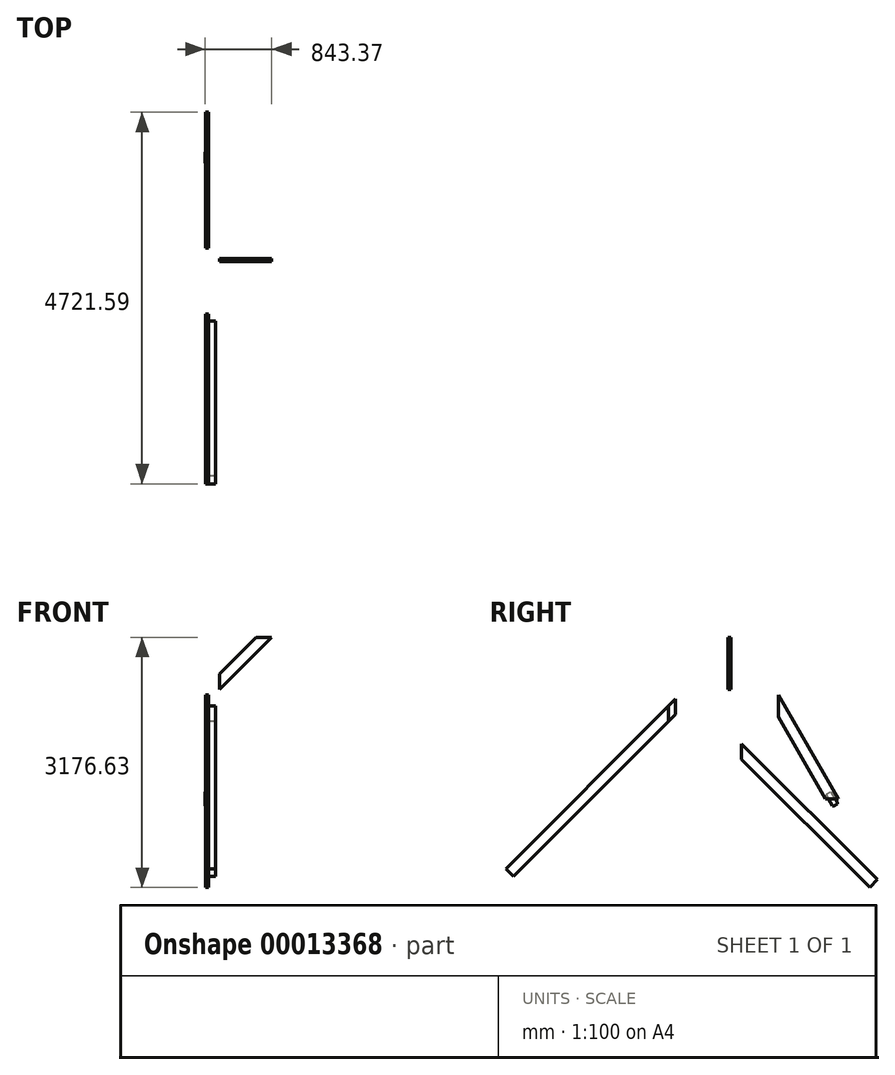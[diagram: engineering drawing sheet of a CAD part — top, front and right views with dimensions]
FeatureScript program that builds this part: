
annotation { "Feature Type Name" : "Feature", "Feature Type Description" : "" }
export const myFeature = defineFeature(function(context is Context, id is Id, definition is map)
    precondition{}
    {
        {
            var Q0;
            Q0=qCreatedBy(makeId("Front.planeOp"),FACE);
            var sketch = newSketch(context, id + "F0", { "sketchPlane" : qUnion([Q0])});
            skLineSegment(sketch, "E0", {"start": v(181.36, 197.57) * mm, "end": v(644.2, 660.4) * mm});
            skLineSegment(sketch, "E1", {"start": v(644.2, 660.4) * mm, "end": v(841.76, 660.4) * mm});
            skLineSegment(sketch, "E2", {"start": v(841.76, 660.4) * mm, "end": v(181.36, 0) * mm});
            skLineSegment(sketch, "E3", {"start": v(181.36, 0) * mm, "end": v(181.36, 197.57) * mm});
            skLineSegment(sketch, "E4", {"start": v(181.36, 0) * mm, "end": v(935.54, 0) * mm, "construction": true});
            skSolve(sketch);
        }
        {
            var Q0;
            Q0=makeQuery(id+"F0.imprint","IMPRINT",FACE,{"disambiguationData":[TD([[makeQuery(id+"F0.imprint","IMPRINT",EDGE,{"derivedFrom":sQuery(id+"F0.wireOp",EDGE,"E0")}),-1.0]])]});
            extrude(context, id + "F1", {"entities" : qUnion([Q0]), "depth" : 38.1 * mm});
        }
        {
            var Q0;
            Q0=qCreatedBy(makeId("Right.planeOp"),FACE);
            var sketch = newSketch(context, id + "F2", { "sketchPlane" : qUnion([Q0])});
            skLineSegment(sketch, "E5", {"start": v(-705.66, -124.36) * mm, "end": v(-705.66, -321.92) * mm});
            skLineSegment(sketch, "E6", {"start": v(-705.66, -321.92) * mm, "end": v(-2762.14, -2378.4) * mm});
            skLineSegment(sketch, "E7", {"start": v(-2762.14, -2378.4) * mm, "end": v(-2860.92, -2279.62) * mm});
            skLineSegment(sketch, "E8", {"start": v(-2860.92, -2279.62) * mm, "end": v(-705.66, -124.36) * mm});
            skSolve(sketch);
        }
        {
            var Q0;
            Q0=qSketchRegion(id+"F2",true);
            extrude(context, id + "F3", {"entities" : qUnion([Q0]), "depth" : 38.1 * mm});
        }
        {
            var Q0;
            Q0=qCreatedBy(makeId("Right.planeOp"),FACE);
            var sketch = newSketch(context, id + "F4", { "sketchPlane" : qUnion([Q0])});
            skLineSegment(sketch, "E9", {"start": v(136.46, -693.23) * mm, "end": v(136.46, -890.8) * mm});
            skLineSegment(sketch, "E10", {"start": v(136.46, -890.8) * mm, "end": v(1761.89, -2516.23) * mm});
            skLineSegment(sketch, "E11", {"start": v(1761.89, -2516.23) * mm, "end": v(1860.67, -2417.44) * mm});
            skLineSegment(sketch, "E12", {"start": v(1860.67, -2417.44) * mm, "end": v(136.46, -693.23) * mm});
            skSolve(sketch);
        }
        {
            var Q0;
            Q0=qSketchRegion(id+"F4",true);
            extrude(context, id + "F5", {"entities" : qUnion([Q0]), "depth" : 38.1 * mm});
        }
        {
            var Q0;
            Q0=qCreatedBy(makeId("Right.planeOp"),FACE);
            var sketch = newSketch(context, id + "F6", { "sketchPlane" : qUnion([Q0])});
            skLineSegment(sketch, "E13", {"start": v(601.15, -72.16) * mm, "end": v(601.15, -351.56) * mm});
            skLineSegment(sketch, "E14", {"start": v(601.15, -351.56) * mm, "end": v(1201.84, -1391.98) * mm});
            skLineSegment(sketch, "E15", {"start": v(1201.84, -1391.98) * mm, "end": v(1363.15, -1391.98) * mm});
            skLineSegment(sketch, "E16", {"start": v(1363.15, -1391.98) * mm, "end": v(601.15, -72.16) * mm});
            skSolve(sketch);
        }
        {
            var Q0;
            Q0=qSketchRegion(id+"F6",true);
            extrude(context, id + "F7", {"entities" : qUnion([Q0]), "depth" : 38.1 * mm});
        }
        {
            var Q0;
            Q0=makeQuery(id+"F7.opExtrude","CAP_FACE",FACE,{"disambiguationData":[OSD([sQuery(id+"F6.wireOp",EDGE,"E13"),sQuery(id+"F6.wireOp",EDGE,"E14"),sQuery(id+"F6.wireOp",EDGE,"E15"),sQuery(id+"F6.wireOp",EDGE,"E16")])],"isStart":true});
            var sketch = newSketch(context, id + "F8", { "sketchPlane" : qUnion([Q0])});
            skLineSegment(sketch, "E17", {"start": v(-1206.16, -1335.97) * mm, "end": v(-1295.06, -1489.95) * mm});
            skLineSegment(sketch, "E18", {"start": v(-1361.05, -1451.85) * mm, "end": v(-1295.06, -1489.95) * mm});
            skLineSegment(sketch, "E19", {"start": v(-1361.05, -1451.85) * mm, "end": v(-1272.15, -1297.87) * mm});
            skLineSegment(sketch, "E20", {"start": v(-1206.16, -1335.97) * mm, "end": v(-1272.15, -1297.87) * mm});
            skLineSegment(sketch, "E21", {"start": v(-1299.65, -1282) * mm, "end": v(-1178.66, -1351.85) * mm, "construction": true});
            skPoint(sketch, "E22", {"position": v(-1239.16, -1316.92) * mm});
            skSolve(sketch);
        }
        {
            var Q0;
            Q0=qSketchRegion(id+"F8",true);
            extrude(context, id + "F9", {"entities" : qUnion([Q0]), "depth" : 1.61 * mm});
        }
        {
            var Q0;
            Q0=makeQuery(id+"F9.opExtrude","SWEPT_EDGE",EDGE,{"disambiguationData":[OSD([sQuery(id+"F8.wireOp",EDGE,"E19"),sQuery(id+"F8.wireOp",EDGE,"E20")])]});
            var Q1;
            Q1=makeQuery(id+"F9.opExtrude","SWEPT_EDGE",EDGE,{"disambiguationData":[OSD([sQuery(id+"F8.wireOp",EDGE,"E17"),sQuery(id+"F8.wireOp",EDGE,"E20")])]});
            var Q2;
            Q2=makeQuery(id+"F9.opExtrude","SWEPT_EDGE",EDGE,{"disambiguationData":[OSD([sQuery(id+"F8.wireOp",EDGE,"E17"),sQuery(id+"F8.wireOp",EDGE,"E18")])]});
            var Q3;
            Q3=makeQuery(id+"F9.opExtrude","SWEPT_EDGE",EDGE,{"disambiguationData":[OSD([sQuery(id+"F8.wireOp",EDGE,"E18"),sQuery(id+"F8.wireOp",EDGE,"E19")])]});
            chamfer(context, id + "F10", {"entities" : qUnion([Q0, Q1, Q2, Q3]), "width" : 12.7 * mm, "tangentPropagation" : true});
        }
        {
            var Q0;
            Q0=makeQuery(id+"F3.opExtrude","CAP_FACE",FACE,{"disambiguationData":[OSD([sQuery(id+"F2.wireOp",EDGE,"E5"),sQuery(id+"F2.wireOp",EDGE,"E6"),sQuery(id+"F2.wireOp",EDGE,"E7"),sQuery(id+"F2.wireOp",EDGE,"E8")])],"isStart":false});
            var sketch = newSketch(context, id + "F11", { "sketchPlane" : qUnion([Q0])});
            skLineSegment(sketch, "E23", {"start": v(-794.56, -213.26) * mm, "end": v(-794.56, -410.82) * mm});
            skLineSegment(sketch, "E24", {"start": v(-794.56, -410.82) * mm, "end": v(-2762.14, -2378.4) * mm});
            skLineSegment(sketch, "E25", {"start": v(-2762.14, -2378.4) * mm, "end": v(-2860.92, -2279.62) * mm});
            skLineSegment(sketch, "E26", {"start": v(-2860.92, -2279.62) * mm, "end": v(-794.56, -213.26) * mm});
            skSolve(sketch);
        }
        {
            var Q0;
            Q0=qSketchRegion(id+"F11",true);
            extrude(context, id + "F12", {"entities" : qUnion([Q0]), "depth" : 88.9 * mm});
        }
    });
